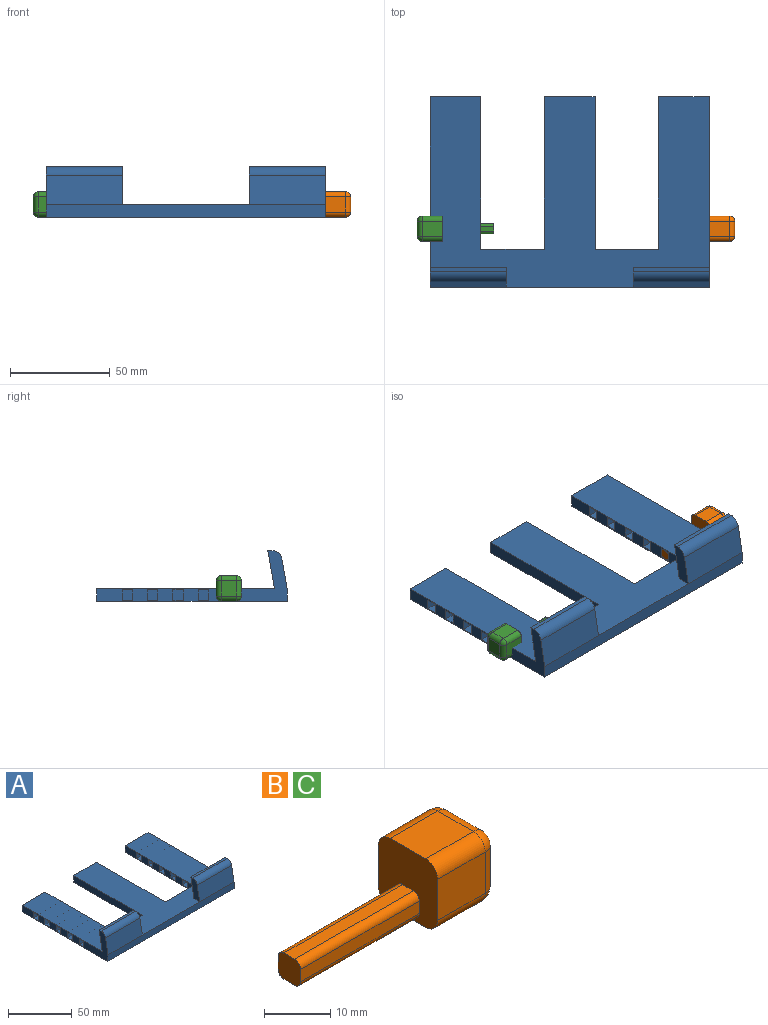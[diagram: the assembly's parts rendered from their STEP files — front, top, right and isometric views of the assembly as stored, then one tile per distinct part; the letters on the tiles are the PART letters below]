
ASSEMBLY  parts=3 mates=1
PART A: 64 faces, bbox 139.7x95.3x25.4 mm
  f0: plane 139.7x95.25mm, normal (0,0,1), area 7983.9mm2, adj f1,f2,f3,f4,f5,f7,f31,f32
  f1: plane 95.25x25.4mm, normal (1,0,0), area 593.1mm2, adj f0,f3,f4,f6,f7,f8,f9,f10
  f2: plane 76.2x6.35mm, normal (-1,0,0), area 354.8mm2, adj f0,f4,f5,f6,f10,f11,f12,f13
  f3: plane 139.7x6.35mm, normal (0,-1,0), area 887.1mm2, adj f0,f1,f6,f9,f34,f40
  f4: plane 25.4x6.35mm, normal (0,1,0), area 161.3mm2, adj f0,f1,f2,f6
  f5: plane 31.75x6.35mm, normal (0,1,0), area 201.6mm2, adj f0,f2,f6,f31
  f6: plane 139.7x95.25mm, normal (0,0,-1), area 8467.7mm2, adj f1,f2,f3,f4,f5,f31,f32,f34
  f7: plane 38.1x19.05mm, normal (0,0.98,-0.17), area 737mm2, adj f0,f1,f8,f33
  f8: plane 38.1x2.09mm, normal (0,0,1), area 79.5mm2, adj f1,f7,f30,f33
  f9: plane 38.1x14.85mm, normal (0,-0.98,0.17), area 574.6mm2, adj f1,f3,f30,f33
  f10: plane 25.4x5.08mm, normal (0,0,-1), area 129mm2, adj f1,f2,f11,f13
  f11: plane 25.4x5.08mm, normal (0,1,0), area 129mm2, adj f1,f2,f10,f12
  f12: plane 25.4x5.08mm, normal (0,0,1), area 129mm2, adj f1,f2,f11,f13
  f13: plane 25.4x5.08mm, normal (0,-1,0), area 129mm2, adj f1,f2,f10,f12
  f14: plane 25.4x5.08mm, normal (0,0,-1), area 129mm2, adj f1,f2,f15,f17
  f15: plane 25.4x5.08mm, normal (0,1,0), area 129mm2, adj f1,f2,f14,f16
  f16: plane 25.4x5.08mm, normal (0,0,1), area 129mm2, adj f1,f2,f15,f17
  f17: plane 25.4x5.08mm, normal (0,-1,0), area 129mm2, adj f1,f2,f14,f16
  f18: plane 25.4x5.08mm, normal (0,0,-1), area 129mm2, adj f1,f2,f19,f21
  f19: plane 25.4x5.08mm, normal (0,1,0), area 129mm2, adj f1,f2,f18,f20
  f20: plane 25.4x5.08mm, normal (0,0,1), area 129mm2, adj f1,f2,f19,f21
  f21: plane 25.4x5.08mm, normal (0,-1,0), area 129mm2, adj f1,f2,f18,f20
  f22: plane 25.4x5.08mm, normal (0,0,-1), area 129mm2, adj f1,f2,f23,f25
  f23: plane 25.4x5.08mm, normal (0,1,0), area 129mm2, adj f1,f2,f22,f24
  f24: plane 25.4x5.08mm, normal (0,0,1), area 129mm2, adj f1,f2,f23,f25
  f25: plane 25.4x5.08mm, normal (0,-1,0), area 129mm2, adj f1,f2,f22,f24
  f26: plane 25.4x5.08mm, normal (0,0,-1), area 129mm2, adj f1,f2,f27,f29
  f27: plane 25.4x5.08mm, normal (0,1,0), area 129mm2, adj f1,f2,f26,f28
  f28: plane 25.4x5.08mm, normal (0,0,1), area 129mm2, adj f1,f2,f27,f29
  f29: plane 25.4x5.08mm, normal (0,-1,0), area 129mm2, adj f1,f2,f26,f28
  f30: cylinder r=5.08mm len=38.1mm, axis (1,0,0), area 270.2mm2, adj f1,f8,f9,f33
  f31: plane 76.2x6.35mm, normal (1,0,0), area 483.9mm2, adj f0,f5,f6,f32
  f32: plane 25.4x6.35mm, normal (0,1,0), area 161.3mm2, adj f0,f6,f31,f62
  f33: plane 19.05x9.71mm, normal (-1,0,0), area 117.3mm2, adj f0,f7,f8,f9,f30
  f34: plane 95.25x25.4mm, normal (-1,0,0), area 593.1mm2, adj f0,f3,f6,f36,f38,f39,f40,f41
  f35: plane 76.2x6.35mm, normal (1,0,0), area 354.8mm2, adj f0,f6,f36,f37,f41,f42,f43,f44
  f36: plane 25.4x6.35mm, normal (0,1,0), area 161.3mm2, adj f0,f6,f34,f35
  f37: plane 31.75x6.35mm, normal (0,1,0), area 201.6mm2, adj f0,f6,f35,f62
  f38: plane 38.1x19.05mm, normal (0,0.98,-0.17), area 737mm2, adj f0,f34,f39,f63
  f39: plane 38.1x2.09mm, normal (0,0,1), area 79.5mm2, adj f34,f38,f61,f63
  f40: plane 38.1x14.85mm, normal (0,-0.98,0.17), area 574.6mm2, adj f3,f34,f61,f63
  f41: plane 25.4x5.08mm, normal (0,0,-1), area 129mm2, adj f34,f35,f42,f44
  f42: plane 25.4x5.08mm, normal (0,1,0), area 129mm2, adj f34,f35,f41,f43
  f43: plane 25.4x5.08mm, normal (0,0,1), area 129mm2, adj f34,f35,f42,f44
  f44: plane 25.4x5.08mm, normal (0,-1,0), area 129mm2, adj f34,f35,f41,f43
  f45: plane 25.4x5.08mm, normal (0,0,-1), area 129mm2, adj f34,f35,f46,f48
  f46: plane 25.4x5.08mm, normal (0,1,0), area 129mm2, adj f34,f35,f45,f47
  f47: plane 25.4x5.08mm, normal (0,0,1), area 129mm2, adj f34,f35,f46,f48
  f48: plane 25.4x5.08mm, normal (0,-1,0), area 129mm2, adj f34,f35,f45,f47
  f49: plane 25.4x5.08mm, normal (0,0,-1), area 129mm2, adj f34,f35,f50,f52
  f50: plane 25.4x5.08mm, normal (0,1,0), area 129mm2, adj f34,f35,f49,f51
  f51: plane 25.4x5.08mm, normal (0,0,1), area 129mm2, adj f34,f35,f50,f52
  f52: plane 25.4x5.08mm, normal (0,-1,0), area 129mm2, adj f34,f35,f49,f51
  f53: plane 25.4x5.08mm, normal (0,0,-1), area 129mm2, adj f34,f35,f54,f56
  f54: plane 25.4x5.08mm, normal (0,1,0), area 129mm2, adj f34,f35,f53,f55
  f55: plane 25.4x5.08mm, normal (0,0,1), area 129mm2, adj f34,f35,f54,f56
  f56: plane 25.4x5.08mm, normal (0,-1,0), area 129mm2, adj f34,f35,f53,f55
  f57: plane 25.4x5.08mm, normal (0,0,-1), area 129mm2, adj f34,f35,f58,f60
  f58: plane 25.4x5.08mm, normal (0,1,0), area 129mm2, adj f34,f35,f57,f59
  f59: plane 25.4x5.08mm, normal (0,0,1), area 129mm2, adj f34,f35,f58,f60
  f60: plane 25.4x5.08mm, normal (0,-1,0), area 129mm2, adj f34,f35,f57,f59
  f61: cylinder r=5.08mm len=38.1mm, axis (-1,0,0), area 270.2mm2, adj f34,f39,f40,f63
  f62: plane 76.2x6.35mm, normal (-1,0,0), area 483.9mm2, adj f0,f6,f32,f37
  f63: plane 19.05x9.71mm, normal (1,0,0), area 117.3mm2, adj f0,f38,f39,f40,f61
PART B: 27 faces, bbox 38.1x12.7x12.7 mm
  f0: plane 25.4x2.29mm, normal (0,0,1), area 58.1mm2, adj f4,f10,f11,f14
  f1: plane 25.4x2.29mm, normal (0,-1,0), area 58.1mm2, adj f4,f10,f11,f12
  f2: plane 25.4x2.29mm, normal (0,0,-1), area 58.1mm2, adj f4,f10,f12,f13
  f3: plane 25.4x2.29mm, normal (0,1,0), area 58.1mm2, adj f4,f10,f13,f14
  f4: plane 4.83x4.83mm, normal (-1,0,0), area 21.9mm2, adj f0,f1,f2,f3,f11,f12,f13,f14
  f5: plane 10.16x7.62mm, normal (0,0,1), area 77.4mm2, adj f10,f17,f23,f26
  f6: plane 10.16x7.62mm, normal (0,-1,0), area 77.4mm2, adj f10,f20,f24,f26
  f7: plane 10.16x7.62mm, normal (0,0,-1), area 77.4mm2, adj f10,f15,f19,f20
  f8: plane 10.16x7.62mm, normal (0,1,0), area 77.4mm2, adj f10,f15,f17,f18
  f9: plane 7.62x7.62mm, normal (1,0,0), area 58.1mm2, adj f18,f19,f23,f24
  f10: plane 12.7x12.7mm, normal (-1,0,0), area 133.8mm2, adj f0,f1,f2,f3,f5,f6,f7,f8
  f11: cylinder r=1.27mm len=25.4mm, axis (1,0,0), area 50.7mm2, adj f0,f1,f4,f10
  f12: cylinder r=1.27mm len=25.4mm, axis (-1,0,0), area 50.7mm2, adj f1,f2,f4,f10
  f13: cylinder r=1.27mm len=25.4mm, axis (1,0,0), area 50.7mm2, adj f2,f3,f4,f10
  f14: cylinder r=1.27mm len=25.4mm, axis (-1,0,0), area 50.7mm2, adj f0,f3,f4,f10
  f15: cylinder r=2.54mm len=10.16mm, axis (1,0,0), area 40.5mm2, adj f7,f8,f10,f16
  f16: sphere r=2.54mm, area 10.1mm2, adj f15,f18,f19
  f17: cylinder r=2.54mm len=10.16mm, axis (-1,0,0), area 40.5mm2, adj f5,f8,f10,f21
  f18: cylinder r=2.54mm len=7.62mm, axis (0,0,-1), area 30.4mm2, adj f8,f9,f16,f21
  f19: cylinder r=2.54mm len=7.62mm, axis (0,-1,0), area 30.4mm2, adj f7,f9,f16,f22
  f20: cylinder r=2.54mm len=10.16mm, axis (-1,0,0), area 40.5mm2, adj f6,f7,f10,f22
  f21: sphere r=2.54mm, area 10.1mm2, adj f17,f18,f23
  f22: sphere r=2.54mm, area 10.1mm2, adj f19,f20,f24
  f23: cylinder r=2.54mm len=7.62mm, axis (0,1,0), area 30.4mm2, adj f5,f9,f21,f25
  f24: cylinder r=2.54mm len=7.62mm, axis (0,0,1), area 30.4mm2, adj f6,f9,f22,f25
  f25: sphere r=2.54mm, area 10.1mm2, adj f23,f24,f26
  f26: cylinder r=2.54mm len=10.16mm, axis (1,0,0), area 40.5mm2, adj f5,f6,f10,f25
PART C: same geometry as B
PLACE A t=(-21.87,-7.54,14.43)mm fixed
PLACE B t=(35.28,-10.84,17.61)mm
PLACE C rot(axis=(0,0,1),180deg) t=(-72.67,-10.84,17.61)mm
MATE slider B.f4 <-> A.f1  axis (-1,0,0) through (22.58,-10.84,17.61)mm
